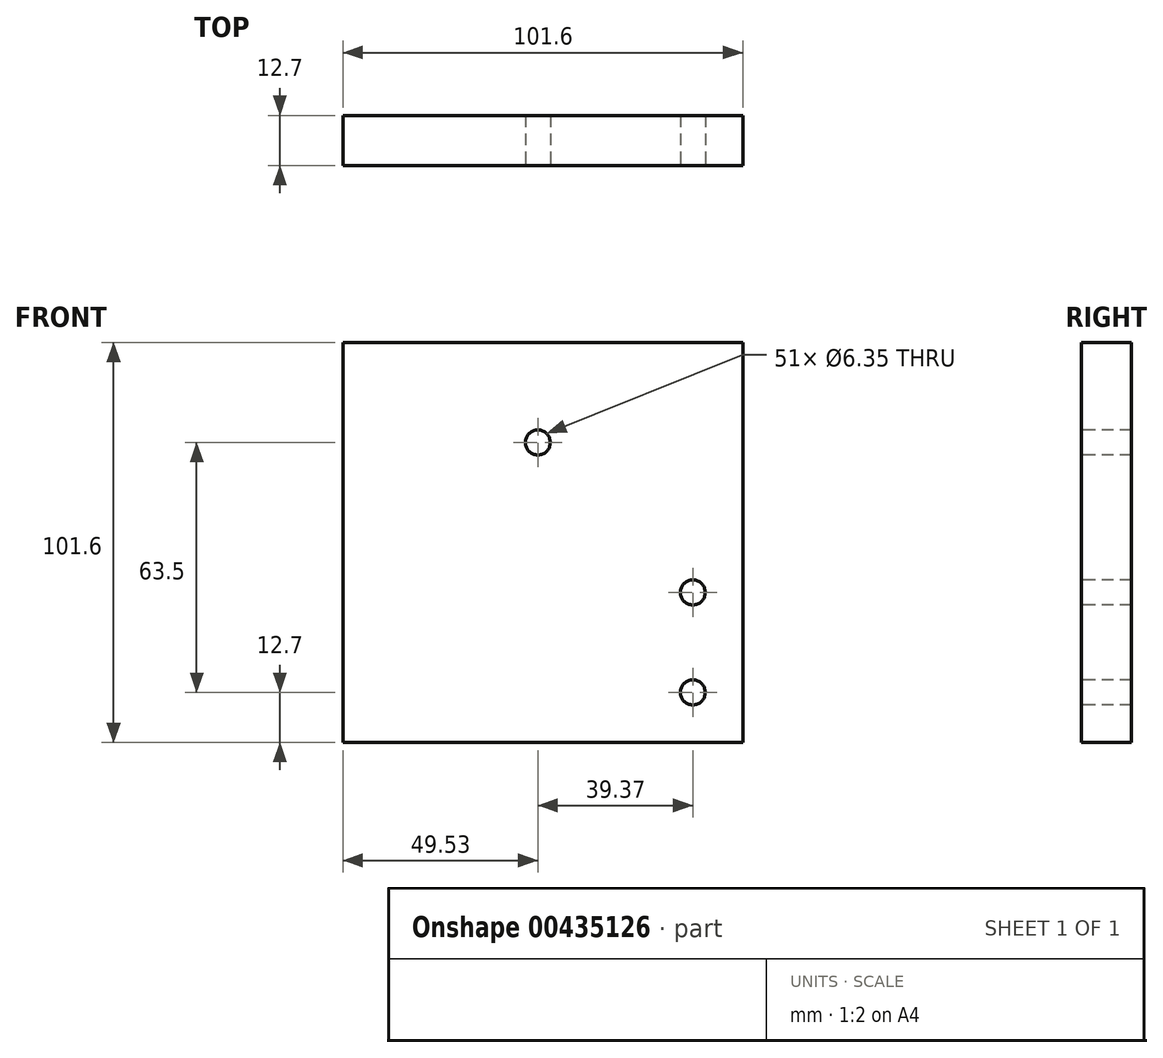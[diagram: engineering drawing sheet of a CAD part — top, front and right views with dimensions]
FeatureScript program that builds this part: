
annotation { "Feature Type Name" : "Feature", "Feature Type Description" : "" }
export const myFeature = defineFeature(function(context is Context, id is Id, definition is map)
    precondition{}
    {
        {
            var Q0;
            Q0=qCreatedBy(makeId("Front.planeOp"),FACE);
            var sketch = newSketch(context, id + "F0", { "sketchPlane" : qUnion([Q0])});
            skLineSegment(sketch, "E0.bottom", {"start": v(0, 0) * mm, "end": v(101.6, 0) * mm});
            skLineSegment(sketch, "E0.top", {"start": v(0, 101.6) * mm, "end": v(101.6, 101.6) * mm});
            skLineSegment(sketch, "E0.left", {"start": v(0, 0) * mm, "end": v(0, 101.6) * mm});
            skLineSegment(sketch, "E0.right", {"start": v(101.6, 0) * mm, "end": v(101.6, 101.6) * mm});
            skSolve(sketch);
        }
        {
            var Q0;
            Q0 = qSketchRegion(id + "F0", true);
            extrude(context, id + "F1", {"entities" : qUnion([Q0]), "depth" : 12.7 * mm});
        }
        {
            var Q0;
            Q0=makeQuery(id+"F1.opExtrude","CAP_FACE",FACE,{"disambiguationData":[OSD([sQuery(id+"F0.wireOp",EDGE,"E0.bottom"),sQuery(id+"F0.wireOp",EDGE,"E0.top"),sQuery(id+"F0.wireOp",EDGE,"E0.left"),sQuery(id+"F0.wireOp",EDGE,"E0.right")])],"isStart":false});
            var sketch = newSketch(context, id + "F2", { "sketchPlane" : qUnion([Q0])});
            skPoint(sketch, "E1", {"position": v(88.9, 12.7) * mm});
            skPoint(sketch, "E2", {"position": v(88.9, 38.1) * mm});
            skPoint(sketch, "E3", {"position": v(49.53, 76.2) * mm});
            skSolve(sketch);
        }
        {
            var Q0;
            Q0=sQuery(id+"F2.wireOp",VERTEX,"E1");
            var Q1;
            Q1=sQuery(id+"F2.wireOp",VERTEX,"E2");
            var Q2;
            Q2=sQuery(id+"F2.wireOp",VERTEX,"E3");
            var Q3;
            Q3=makeQuery(id+"F1.opExtrude","SWEPT_BODY",BODY,{"disambiguationData":[OSD([sQuery(id+"F0.wireOp",EDGE,"E0.bottom"),sQuery(id+"F0.wireOp",EDGE,"E0.top"),sQuery(id+"F0.wireOp",EDGE,"E0.left"),sQuery(id+"F0.wireOp",EDGE,"E0.right")])]});
            hole(context, id + "F3", {"style" : HoleStyle.SIMPLE, "endStyle" : HoleEndStyle.THROUGH, "holeDiameter" : 6.35 * mm, "isTappedThrough" : true, "tappedDepth" : 12.7 * mm, "tapClearance" : 3, "locations" : qUnion([Q0, Q1, Q2]), "scope" : qUnion([Q3])});
        }
    });
